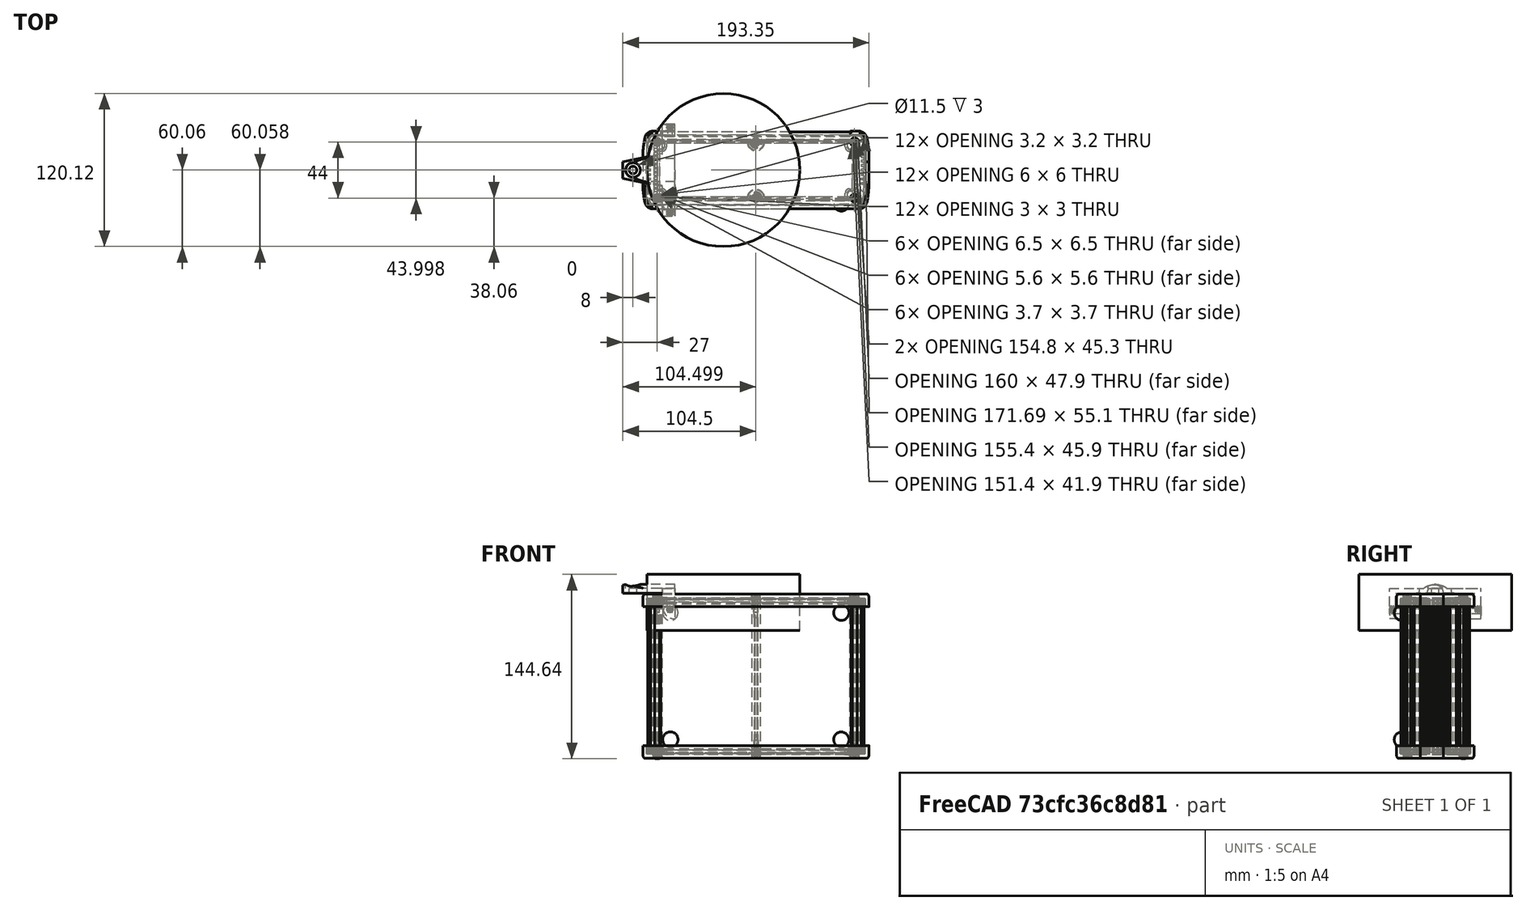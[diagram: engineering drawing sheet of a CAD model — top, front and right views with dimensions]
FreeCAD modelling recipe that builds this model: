
FCSTD DOCUMENT  (FreeCAD 0.20R29410 (Git))
Label: antennaHolder2022_11_14
License: All rights reserved
LicenseURL: http://en.wikipedia.org/wiki/All_rights_reserved
objects: Part::Cylinder×8, Part::MultiFuse×5, Part::Box×4, Part::Feature×3, Part::Cut×3, Part::Cone×1, Part::MultiCommon×1
note: 25 computed .brp shape members not serialized (recipe doc carries the construction recipe); baked Part::Feature solids carry a one-line shape summary decoded from their .brp

FEATURE [Part::Feature] Feature  label="EX-64-002"
  Placement = pos=(73.5,0,0) rot=(0,0,1;0rad)
  shape: bbox 178.8 x 63.35 x 129.6 mm, 1628 faces, 33 solids (baked)
FEATURE [Part::Box] Box  label="out"
  AttacherType = Attacher::AttachEngine3D
  Height = 24
  Length = 10
  Placement = pos=(0,-36,45) rot=(0,0,1;0rad)
  Width = 72
FEATURE [Part::Box] Box001  label="in"
  AttacherType = Attacher::AttachEngine3D
  Height = 11
  Length = 10
  Placement = pos=(0,-31,54) rot=(0,0,1;0rad)
  Width = 62
FEATURE [Part::Box] Box002  label="in001"
  AttacherType = Attacher::AttachEngine3D
  Height = 11
  Length = 10
  Placement = pos=(0,-27,45) rot=(0,0,1;0rad)
  Width = 54
FEATURE [Part::MultiFuse] Fusion  label="in002"
  Shapes = -> [Box001,Box002]
FEATURE [Part::Cut] Cut
  Base = -> Box
  Tool = -> Fusion
FEATURE [Part::Feature] Solid  label="m3HeatSetInsert"
  Placement = pos=(6,31.5,52.5) rot=(0,0,1;0rad)
  shape: bbox 4.772 x 4.354 x 4.772 mm, 239 faces (baked)
FEATURE [Part::Cylinder] Cylinder
  Angle = 90
  AttacherType = Attacher::AttachEngine3D
  FirstAngle = 0
  Height = 5
  Placement = pos=(10,31,55) rot=(0.57735,-0.57735,-0.57735;4.18879rad)
  Radius = 10
  SecondAngle = 0
FEATURE [Part::Feature] Solid001  label="m3HeatSetInsert001"
  Placement = pos=(6,-31,52.5) rot=(0,0,1;3.14159rad)
  shape: bbox 4.772 x 4.354 x 4.772 mm, 239 faces (baked)
FEATURE [Part::Cylinder] Cylinder001
  Angle = 90
  AttacherType = Attacher::AttachEngine3D
  FirstAngle = 0
  Height = 5
  Placement = pos=(10,-31,55) rot=(0,0.707107,-0.707107;3.14159rad)
  Radius = 10
  SecondAngle = 0
FEATURE [Part::MultiFuse] Fusion001  label="out001"
  Shapes = -> [Cylinder,Cylinder001,Cut]
FEATURE [Part::Cylinder] Cylinder014  label="antennaIn001"
  Angle = 360
  AttacherType = Attacher::AttachEngine3D
  FirstAngle = 0
  Height = 10
  Placement = pos=(-23,0,69) rot=(0,0,1;0rad)
  Radius = 5.75
  SecondAngle = 0
FEATURE [Part::Cylinder] Cylinder013  label="antennaIn"
  Angle = 360
  AttacherType = Attacher::AttachEngine3D
  FirstAngle = 0
  Height = 10
  Placement = pos=(-23,0,65) rot=(0,0,1;0rad)
  Radius = 3
  SecondAngle = 0
FEATURE [Part::MultiFuse] Fusion003
  Shapes = -> [Cylinder013,Cylinder014]
FEATURE [Part::Cylinder] Cylinder016  label="m3HeastSetCut"
  Angle = 360
  AttacherType = Attacher::AttachEngine3D
  FirstAngle = 0
  Height = 94
  Placement = pos=(6,-47.35,51) rot=(-1,0,0;1.5708rad)
  Radius = 2
  SecondAngle = 0
FEATURE [Part::Cylinder] Cylinder017  label="include001"
  Angle = 90
  AttacherType = Attacher::AttachEngine3D
  FirstAngle = 0
  Height = 87
  Placement = pos=(10,-40.75,55) rot=(0.57735,-0.57735,-0.57735;4.18879rad)
  Radius = 10
  SecondAngle = 0
FEATURE [Part::Box] Box004  label="include"
  AttacherType = Attacher::AttachEngine3D
  Height = 14
  Length = 42
  Placement = pos=(-31,-36,55) rot=(0,0,1;0rad)
  Width = 82
FEATURE [Part::Cylinder] Cylinder018
  Angle = 360
  AttacherType = Attacher::AttachEngine3D
  FirstAngle = 0
  Height = 42
  Placement = pos=(-31,0,57) rot=(0.57735,0.57735,0.57735;2.0944rad)
  Radius = 15
  SecondAngle = 0
FEATURE [Part::Cylinder] Cylinder019
  Angle = 360
  AttacherType = Attacher::AttachEngine3D
  FirstAngle = 0
  Height = 44
  Placement = pos=(48,0,35.9) rot=(0,0,1;0rad)
  Radius = 60.06
  SecondAngle = 0
FEATURE [Part::Cone] Cone
  Angle = 180
  AttacherType = Attacher::AttachEngine3D
  Height = 41
  Placement = pos=(10,-2e-15,65) rot=(-0.57735,0.57735,0.57735;4.18879rad)
  Radius1 = 15
  Radius2 = 6.5
FEATURE [Part::MultiFuse] Fusion004
  Shapes = -> [Fusion001,Cone]
FEATURE [Part::Cut] Cut001
  Base = -> Fusion004
  Tool = -> Cylinder016
FEATURE [Part::Cut] Cut002
  Base = -> Cut001
  Tool = -> Fusion003
FEATURE [Part::MultiFuse] Fusion005  label="include002"
  Shapes = -> [Cylinder018,Box004,Cylinder017]
FEATURE [Part::MultiCommon] Common
  Shapes = -> [Cut002,Fusion005]
